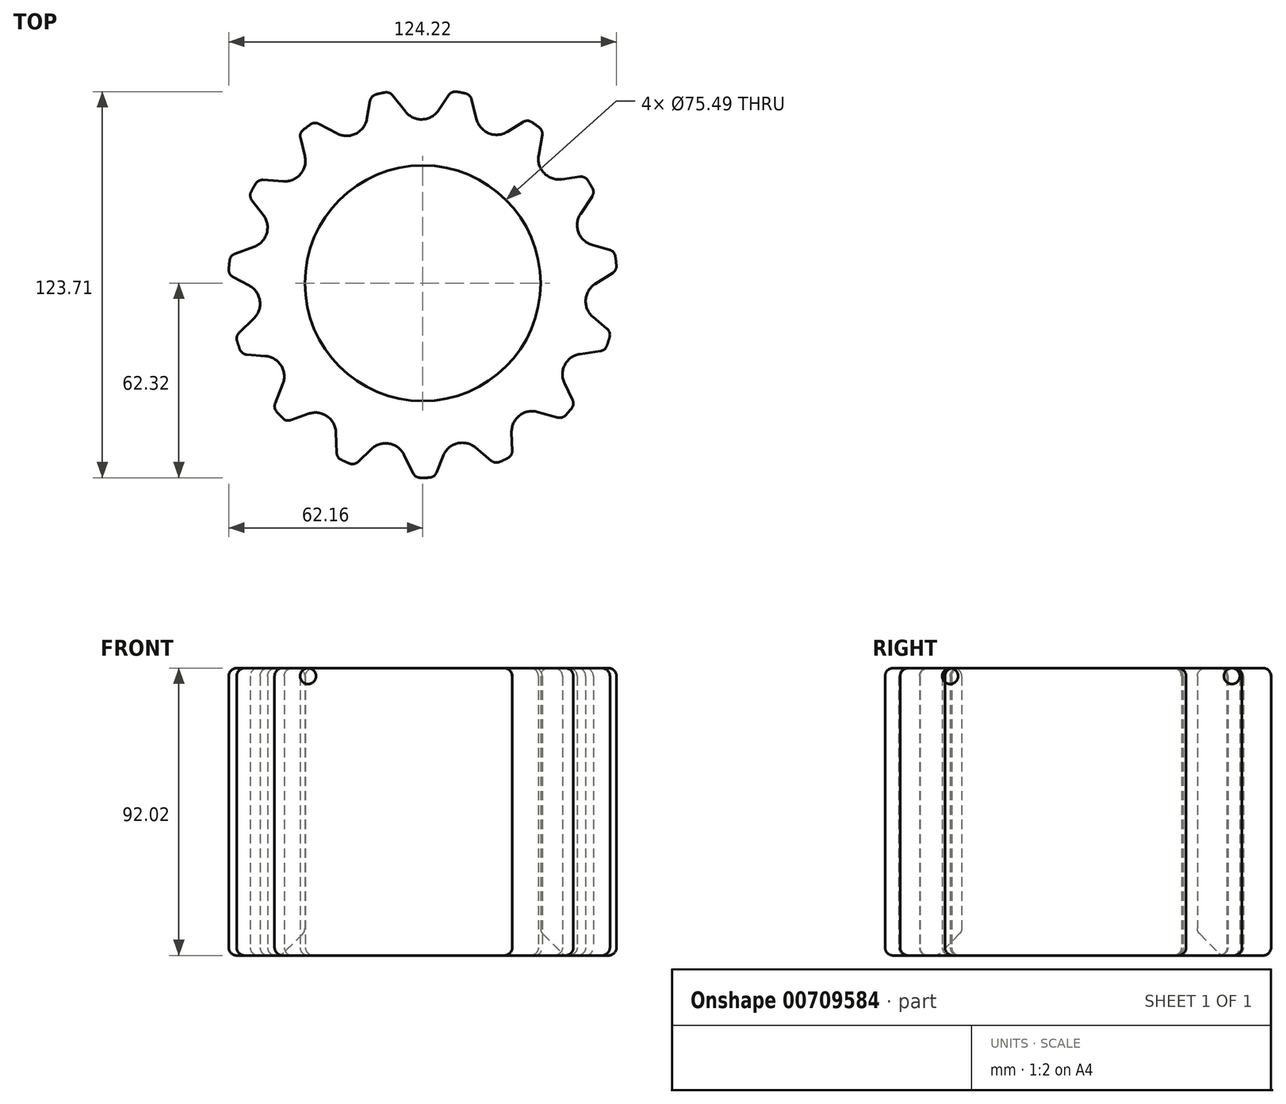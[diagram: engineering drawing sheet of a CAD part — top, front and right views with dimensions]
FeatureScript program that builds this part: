
annotation { "Feature Type Name" : "Feature", "Feature Type Description" : "" }
export const myFeature = defineFeature(function(context is Context, id is Id, definition is map)
    precondition{}
    {
        {
            var Q0;
            Q0=qCreatedBy(makeId("Top.planeOp"),FACE);
            var sketch = newSketch(context, id + "F0", { "sketchPlane" : qUnion([Q0])});
            skCircle(sketch, "E0", {"center": v(0, 0) * mm, "radius": 62.32 * mm});
            skLineSegment(sketch, "E1", {"start": v(-10.63, 61.4) * mm, "end": v(-5.56, 54.98) * mm});
            skLineSegment(sketch, "E2", {"start": v(5.04, 55.37) * mm, "end": v(9.28, 61.62) * mm});
            skLineSegment(sketch, "E3", {"start": v(9.28, 61.62) * mm, "end": v(9.28, 61.62) * mm});
            skPoint(sketch, "E4.visualSharp", {"position": v(0, 47.95) * mm});
            skArc(sketch, "E4.filletArc", {"start": v(-5.56, 54.98) * mm, "mid": v(-0.16, 52.5) * mm, "end": v(5.04, 55.37) * mm});
            skLineSegment(sketch, "E5", {"start": v(0, 113.38) * mm, "end": v(0, -82.74) * mm});
            skLineSegment(sketch, "E6", {"start": v(93.43, 0) * mm, "end": v(-91.25, 0) * mm});
            skLineSegment(sketch, "E7.anchor1", {"start": v(0, 0) * mm, "end": v(-5.56, 54.98) * mm, "construction": true});
            skLineSegment(sketch, "E7.anchor2", {"start": v(0, 0) * mm, "end": v(-5.56, 54.98) * mm, "construction": true});
            skArc(sketch, "E8.1.0", {"start": v(17.29, 52.5) * mm, "mid": v(21.2, 48.02) * mm, "end": v(27.12, 48.53) * mm});
            skLineSegment(sketch, "E8.1.1", {"start": v(27.12, 48.53) * mm, "end": v(33.54, 52.52) * mm});
            skLineSegment(sketch, "E8.1.2", {"start": v(15.26, 60.42) * mm, "end": v(17.29, 52.5) * mm});
            skArc(sketch, "E8.2.0", {"start": v(37.14, 40.92) * mm, "mid": v(38.9, 35.25) * mm, "end": v(44.52, 33.3) * mm});
            skLineSegment(sketch, "E8.2.1", {"start": v(44.52, 33.3) * mm, "end": v(52, 34.33) * mm});
            skLineSegment(sketch, "E8.2.2", {"start": v(38.52, 48.99) * mm, "end": v(37.14, 40.92) * mm});
            skArc(sketch, "E8.3.0", {"start": v(50.58, 22.28) * mm, "mid": v(49.87, 16.38) * mm, "end": v(54.21, 12.32) * mm});
            skLineSegment(sketch, "E8.3.1", {"start": v(54.21, 12.32) * mm, "end": v(61.47, 10.21) * mm});
            skLineSegment(sketch, "E8.3.2", {"start": v(55.11, 29.08) * mm, "end": v(50.58, 22.28) * mm});
            skArc(sketch, "E8.4.0", {"start": v(55.26, -0.22) * mm, "mid": v(52.22, -5.32) * mm, "end": v(54.54, -10.8) * mm});
            skLineSegment(sketch, "E8.4.1", {"start": v(54.54, -10.8) * mm, "end": v(60.31, -15.67) * mm});
            skLineSegment(sketch, "E8.4.2", {"start": v(62.18, 4.15) * mm, "end": v(55.26, -0.22) * mm});
            skArc(sketch, "E8.5.0", {"start": v(50.4, -22.68) * mm, "mid": v(45.54, -26.1) * mm, "end": v(45.43, -32.04) * mm});
            skLineSegment(sketch, "E8.5.1", {"start": v(45.43, -32.04) * mm, "end": v(48.72, -38.85) * mm});
            skLineSegment(sketch, "E8.5.2", {"start": v(58.5, -21.5) * mm, "end": v(50.4, -22.68) * mm});
            skArc(sketch, "E8.6.0", {"start": v(36.82, -41.22) * mm, "mid": v(30.99, -42.37) * mm, "end": v(28.47, -47.75) * mm});
            skLineSegment(sketch, "E8.6.1", {"start": v(28.47, -47.75) * mm, "end": v(28.71, -55.3) * mm});
            skLineSegment(sketch, "E8.6.2", {"start": v(44.7, -43.43) * mm, "end": v(36.82, -41.22) * mm});
            skArc(sketch, "E8.7.0", {"start": v(16.87, -52.63) * mm, "mid": v(11.07, -51.31) * mm, "end": v(6.59, -55.2) * mm});
            skLineSegment(sketch, "E8.7.1", {"start": v(6.59, -55.2) * mm, "end": v(3.73, -62.2) * mm});
            skLineSegment(sketch, "E8.7.2", {"start": v(23.16, -57.85) * mm, "end": v(16.87, -52.63) * mm});
            skArc(sketch, "E8.8.0", {"start": v(-6, -54.94) * mm, "mid": v(-10.75, -51.38) * mm, "end": v(-16.44, -53.11) * mm});
            skLineSegment(sketch, "E8.8.1", {"start": v(-16.44, -53.11) * mm, "end": v(-21.9, -58.34) * mm});
            skLineSegment(sketch, "E8.8.2", {"start": v(-2.37, -62.27) * mm, "end": v(-6, -54.94) * mm});
            skArc(sketch, "E8.9.0", {"start": v(-27.82, -47.75) * mm, "mid": v(-30.72, -42.56) * mm, "end": v(-36.62, -41.83) * mm});
            skLineSegment(sketch, "E8.9.1", {"start": v(-36.62, -41.83) * mm, "end": v(-43.73, -44.4) * mm});
            skLineSegment(sketch, "E8.9.2", {"start": v(-27.5, -55.92) * mm, "end": v(-27.82, -47.75) * mm});
            skArc(sketch, "E8.10.0", {"start": v(-44.84, -32.3) * mm, "mid": v(-45.38, -26.39) * mm, "end": v(-50.47, -23.32) * mm});
            skLineSegment(sketch, "E8.10.1", {"start": v(-50.47, -23.32) * mm, "end": v(-58, -22.77) * mm});
            skLineSegment(sketch, "E8.10.2", {"start": v(-47.86, -39.9) * mm, "end": v(-44.84, -32.3) * mm});
            skArc(sketch, "E8.11.0", {"start": v(-54.1, -11.27) * mm, "mid": v(-52.19, -5.65) * mm, "end": v(-55.6, -0.78) * mm});
            skLineSegment(sketch, "E8.11.1", {"start": v(-55.6, -0.78) * mm, "end": v(-62.25, 2.79) * mm});
            skLineSegment(sketch, "E8.11.2", {"start": v(-59.96, -16.99) * mm, "end": v(-54.1, -11.27) * mm});
            skArc(sketch, "E8.12.0", {"start": v(-54.01, 11.7) * mm, "mid": v(-49.97, 16.06) * mm, "end": v(-51.1, 21.9) * mm});
            skLineSegment(sketch, "E8.12.1", {"start": v(-51.1, 21.9) * mm, "end": v(-55.74, 27.87) * mm});
            skLineSegment(sketch, "E8.12.2", {"start": v(-61.68, 8.87) * mm, "end": v(-54.01, 11.7) * mm});
            skArc(sketch, "E8.13.0", {"start": v(-44.58, 32.66) * mm, "mid": v(-39.12, 35) * mm, "end": v(-37.78, 40.8) * mm});
            skLineSegment(sketch, "E8.13.1", {"start": v(-37.78, 40.8) * mm, "end": v(-39.58, 48.13) * mm});
            skLineSegment(sketch, "E8.13.2", {"start": v(-52.74, 33.19) * mm, "end": v(-44.58, 32.66) * mm});
            skArc(sketch, "E8.14.0", {"start": v(-27.44, 47.97) * mm, "mid": v(-21.5, 47.89) * mm, "end": v(-17.92, 52.63) * mm});
            skLineSegment(sketch, "E8.14.1", {"start": v(-17.92, 52.63) * mm, "end": v(-16.58, 60.07) * mm});
            skLineSegment(sketch, "E8.14.2", {"start": v(-34.69, 51.77) * mm, "end": v(-27.44, 47.97) * mm});
            skCircle(sketch, "E9", {"center": v(0, 0) * mm, "radius": 37.75 * mm});
            skSolve(sketch);
        }
        {
            var Q0;
            {var subQ1=sQuery(id+"F0.wireOp",EDGE,"E8.4.0");Q0=makeQuery(id+"F0.imprint","IMPRINT",FACE,{"disambiguationData":[TD([[makeQuery(id+"F0.imprint","IMPRINT",EDGE,{"derivedFrom":subQ1}),-1.0]])]});}
            var Q1;
            Q1=makeQuery(id+"F0.imprint","IMPRINT",FACE,{"disambiguationData":[TD([[makeQuery(id+"F0.imprint","IMPRINT",EDGE,{"derivedFrom":sQuery(id+"F0.wireOp",EDGE,"E8.8.0")}),-1.0]])]});
            var Q2;
            Q2=makeQuery(id+"F0.imprint","IMPRINT",FACE,{"disambiguationData":[TD([[makeQuery(id+"F0.imprint","IMPRINT",EDGE,{"derivedFrom":sQuery(id+"F0.wireOp",EDGE,"E8.1.0")}),-1.0]])]});
            var Q3;
            Q3=makeQuery(id+"F0.imprint","IMPRINT",FACE,{"disambiguationData":[TD([[makeQuery(id+"F0.imprint","IMPRINT",EDGE,{"derivedFrom":sQuery(id+"F0.wireOp",EDGE,"E8.12.0")}),-1.0]])]});
            extrude(context, id + "F1", {"entities" : qUnion([Q0, Q1, Q2, Q3]), "depth" : 92.02 * mm, "offsetDistance" : 25.4 * mm});
        }
        {
            var Q0;
            Q0=makeQuery(id+"F1.opExtrude","CAP_EDGE",EDGE,{"disambiguationData":[OSD([sQuery(id+"F0.wireOp",EDGE,"E9")])],"isStart":true});
            chamfer(context, id + "F2", {"entities" : qUnion([Q0]), "width" : 7.62 * mm, "tangentPropagation" : true});
        }
        {
            var Q0;
            Q0=makeQuery(id+"F1.opExtrude","SWEPT_EDGE",EDGE,{"disambiguationData":[OSD([sQuery(id+"F0.wireOp",EDGE,"E0"),sQuery(id+"F0.wireOp",EDGE,"E8.12.2")])]});
            var Q1;
            Q1=makeQuery(id+"F1.opExtrude","SWEPT_EDGE",EDGE,{"disambiguationData":[OSD([sQuery(id+"F0.wireOp",EDGE,"E0"),sQuery(id+"F0.wireOp",EDGE,"E8.11.1")])]});
            var Q2;
            Q2=makeQuery(id+"F1.opExtrude","SWEPT_EDGE",EDGE,{"disambiguationData":[OSD([sQuery(id+"F0.wireOp",EDGE,"E0"),sQuery(id+"F0.wireOp",EDGE,"E8.12.1")])]});
            var Q3;
            Q3=makeQuery(id+"F1.opExtrude","SWEPT_EDGE",EDGE,{"disambiguationData":[OSD([sQuery(id+"F0.wireOp",EDGE,"E0"),sQuery(id+"F0.wireOp",EDGE,"E8.13.2")])]});
            var Q4;
            Q4=makeQuery(id+"F1.opExtrude","SWEPT_EDGE",EDGE,{"disambiguationData":[OSD([sQuery(id+"F0.wireOp",EDGE,"E0"),sQuery(id+"F0.wireOp",EDGE,"E8.13.1")])]});
            var Q5;
            Q5=makeQuery(id+"F1.opExtrude","SWEPT_EDGE",EDGE,{"disambiguationData":[OSD([sQuery(id+"F0.wireOp",EDGE,"E0"),sQuery(id+"F0.wireOp",EDGE,"E8.14.2")])]});
            var Q6;
            Q6=makeQuery(id+"F1.opExtrude","SWEPT_EDGE",EDGE,{"disambiguationData":[OSD([sQuery(id+"F0.wireOp",EDGE,"E0"),sQuery(id+"F0.wireOp",EDGE,"E8.14.1")])]});
            var Q7;
            Q7=makeQuery(id+"F1.opExtrude","SWEPT_EDGE",EDGE,{"disambiguationData":[OSD([sQuery(id+"F0.wireOp",EDGE,"E0"),sQuery(id+"F0.wireOp",EDGE,"E1")])]});
            var Q8;
            Q8=makeQuery(id+"F1.opExtrude","SWEPT_EDGE",EDGE,{"disambiguationData":[OSD([sQuery(id+"F0.wireOp",EDGE,"E0"),sQuery(id+"F0.wireOp",EDGE,"E2")])]});
            var Q9;
            Q9=makeQuery(id+"F1.opExtrude","SWEPT_EDGE",EDGE,{"disambiguationData":[OSD([sQuery(id+"F0.wireOp",EDGE,"E0"),sQuery(id+"F0.wireOp",EDGE,"E8.1.2")])]});
            var Q10;
            Q10=makeQuery(id+"F1.opExtrude","SWEPT_EDGE",EDGE,{"disambiguationData":[OSD([sQuery(id+"F0.wireOp",EDGE,"E0"),sQuery(id+"F0.wireOp",EDGE,"E8.1.1")])]});
            var Q11;
            Q11=makeQuery(id+"F1.opExtrude","SWEPT_EDGE",EDGE,{"disambiguationData":[OSD([sQuery(id+"F0.wireOp",EDGE,"E0"),sQuery(id+"F0.wireOp",EDGE,"E8.2.2")])]});
            var Q12;
            Q12=makeQuery(id+"F1.opExtrude","SWEPT_EDGE",EDGE,{"disambiguationData":[OSD([sQuery(id+"F0.wireOp",EDGE,"E0"),sQuery(id+"F0.wireOp",EDGE,"E8.3.2")])]});
            var Q13;
            Q13=makeQuery(id+"F1.opExtrude","SWEPT_EDGE",EDGE,{"disambiguationData":[OSD([sQuery(id+"F0.wireOp",EDGE,"E0"),sQuery(id+"F0.wireOp",EDGE,"E8.2.1")])]});
            var Q14;
            Q14=makeQuery(id+"F1.opExtrude","SWEPT_EDGE",EDGE,{"disambiguationData":[OSD([sQuery(id+"F0.wireOp",EDGE,"E0"),sQuery(id+"F0.wireOp",EDGE,"E8.3.1")])]});
            var Q15;
            Q15=makeQuery(id+"F1.opExtrude","SWEPT_EDGE",EDGE,{"disambiguationData":[OSD([sQuery(id+"F0.wireOp",EDGE,"E0"),sQuery(id+"F0.wireOp",EDGE,"E8.4.2")])]});
            var Q16;
            Q16=makeQuery(id+"F1.opExtrude","SWEPT_EDGE",EDGE,{"disambiguationData":[OSD([sQuery(id+"F0.wireOp",EDGE,"E0"),sQuery(id+"F0.wireOp",EDGE,"E8.4.1")])]});
            var Q17;
            Q17=makeQuery(id+"F1.opExtrude","SWEPT_EDGE",EDGE,{"disambiguationData":[OSD([sQuery(id+"F0.wireOp",EDGE,"E0"),sQuery(id+"F0.wireOp",EDGE,"E8.5.2")])]});
            var Q18;
            Q18=makeQuery(id+"F1.opExtrude","SWEPT_EDGE",EDGE,{"disambiguationData":[OSD([sQuery(id+"F0.wireOp",EDGE,"E0"),sQuery(id+"F0.wireOp",EDGE,"E8.6.2")])]});
            var Q19;
            Q19=makeQuery(id+"F1.opExtrude","SWEPT_EDGE",EDGE,{"disambiguationData":[OSD([sQuery(id+"F0.wireOp",EDGE,"E0"),sQuery(id+"F0.wireOp",EDGE,"E8.5.1")])]});
            var Q20;
            Q20=makeQuery(id+"F1.opExtrude","SWEPT_EDGE",EDGE,{"disambiguationData":[OSD([sQuery(id+"F0.wireOp",EDGE,"E0"),sQuery(id+"F0.wireOp",EDGE,"E8.6.1")])]});
            var Q21;
            Q21=makeQuery(id+"F1.opExtrude","SWEPT_EDGE",EDGE,{"disambiguationData":[OSD([sQuery(id+"F0.wireOp",EDGE,"E0"),sQuery(id+"F0.wireOp",EDGE,"E8.7.2")])]});
            var Q22;
            Q22=makeQuery(id+"F1.opExtrude","SWEPT_EDGE",EDGE,{"disambiguationData":[OSD([sQuery(id+"F0.wireOp",EDGE,"E0"),sQuery(id+"F0.wireOp",EDGE,"E8.7.1")])]});
            var Q23;
            Q23=makeQuery(id+"F1.opExtrude","SWEPT_EDGE",EDGE,{"disambiguationData":[OSD([sQuery(id+"F0.wireOp",EDGE,"E0"),sQuery(id+"F0.wireOp",EDGE,"E8.8.2")])]});
            var Q24;
            Q24=makeQuery(id+"F1.opExtrude","SWEPT_EDGE",EDGE,{"disambiguationData":[OSD([sQuery(id+"F0.wireOp",EDGE,"E0"),sQuery(id+"F0.wireOp",EDGE,"E8.9.2")])]});
            var Q25;
            Q25=makeQuery(id+"F1.opExtrude","SWEPT_EDGE",EDGE,{"disambiguationData":[OSD([sQuery(id+"F0.wireOp",EDGE,"E0"),sQuery(id+"F0.wireOp",EDGE,"E8.8.1")])]});
            var Q26;
            Q26=makeQuery(id+"F1.opExtrude","SWEPT_EDGE",EDGE,{"disambiguationData":[OSD([sQuery(id+"F0.wireOp",EDGE,"E0"),sQuery(id+"F0.wireOp",EDGE,"E8.9.1")])]});
            var Q27;
            Q27=makeQuery(id+"F1.opExtrude","SWEPT_EDGE",EDGE,{"disambiguationData":[OSD([sQuery(id+"F0.wireOp",EDGE,"E0"),sQuery(id+"F0.wireOp",EDGE,"E8.10.2")])]});
            var Q28;
            Q28=makeQuery(id+"F1.opExtrude","SWEPT_EDGE",EDGE,{"disambiguationData":[OSD([sQuery(id+"F0.wireOp",EDGE,"E0"),sQuery(id+"F0.wireOp",EDGE,"E8.10.1")])]});
            var Q29;
            Q29=makeQuery(id+"F1.opExtrude","SWEPT_EDGE",EDGE,{"disambiguationData":[OSD([sQuery(id+"F0.wireOp",EDGE,"E0"),sQuery(id+"F0.wireOp",EDGE,"E8.11.2")])]});
            fillet(context, id + "F3", {"entities" : qUnion([Q0, Q1, Q2, Q3, Q4, Q5, Q6, Q7, Q8, Q9, Q10, Q11, Q12, Q13, Q14, Q15, Q16, Q17, Q18, Q19, Q20, Q21, Q22, Q23, Q24, Q25, Q26, Q27, Q28, Q29]), "radius" : 2.54 * mm, "tangentPropagation" : true, "allowEdgeOverflow" : false});
        }
        {
            var Q0;
            Q0=makeQuery(id+"F1.opExtrude","CAP_FACE",FACE,{"disambiguationData":[OSD([sQuery(id+"F0.wireOp",EDGE,"E0"),sQuery(id+"F0.wireOp",EDGE,"E8.1.0"),sQuery(id+"F0.wireOp",EDGE,"E8.1.1"),sQuery(id+"F0.wireOp",EDGE,"E8.1.2"),sQuery(id+"F0.wireOp",EDGE,"E8.2.0"),sQuery(id+"F0.wireOp",EDGE,"E8.2.1"),sQuery(id+"F0.wireOp",EDGE,"E8.2.2"),sQuery(id+"F0.wireOp",EDGE,"E8.3.0"),sQuery(id+"F0.wireOp",EDGE,"E8.3.1"),sQuery(id+"F0.wireOp",EDGE,"E8.3.2"),sQuery(id+"F0.wireOp",EDGE,"E8.4.0"),sQuery(id+"F0.wireOp",EDGE,"E8.4.1"),sQuery(id+"F0.wireOp",EDGE,"E8.4.2"),sQuery(id+"F0.wireOp",EDGE,"E8.5.0"),sQuery(id+"F0.wireOp",EDGE,"E8.5.1"),sQuery(id+"F0.wireOp",EDGE,"E8.5.2"),sQuery(id+"F0.wireOp",EDGE,"E8.6.0"),sQuery(id+"F0.wireOp",EDGE,"E8.6.1"),sQuery(id+"F0.wireOp",EDGE,"E8.6.2"),sQuery(id+"F0.wireOp",EDGE,"E8.7.0"),sQuery(id+"F0.wireOp",EDGE,"E8.7.1"),sQuery(id+"F0.wireOp",EDGE,"E8.7.2"),sQuery(id+"F0.wireOp",EDGE,"E8.8.0"),sQuery(id+"F0.wireOp",EDGE,"E8.8.1"),sQuery(id+"F0.wireOp",EDGE,"E8.8.2"),sQuery(id+"F0.wireOp",EDGE,"E8.9.0"),sQuery(id+"F0.wireOp",EDGE,"E8.9.1"),sQuery(id+"F0.wireOp",EDGE,"E8.9.2"),sQuery(id+"F0.wireOp",EDGE,"E8.10.0"),sQuery(id+"F0.wireOp",EDGE,"E8.10.1"),sQuery(id+"F0.wireOp",EDGE,"E8.10.2"),sQuery(id+"F0.wireOp",EDGE,"E8.11.0"),sQuery(id+"F0.wireOp",EDGE,"E8.11.1"),sQuery(id+"F0.wireOp",EDGE,"E8.11.2"),sQuery(id+"F0.wireOp",EDGE,"E8.12.0"),sQuery(id+"F0.wireOp",EDGE,"E8.12.1"),sQuery(id+"F0.wireOp",EDGE,"E8.12.2"),sQuery(id+"F0.wireOp",EDGE,"E8.13.0"),sQuery(id+"F0.wireOp",EDGE,"E8.13.1"),sQuery(id+"F0.wireOp",EDGE,"E8.13.2"),sQuery(id+"F0.wireOp",EDGE,"E8.14.0"),sQuery(id+"F0.wireOp",EDGE,"E8.14.1"),sQuery(id+"F0.wireOp",EDGE,"E8.14.2"),sQuery(id+"F0.wireOp",EDGE,"E4.filletArc"),sQuery(id+"F0.wireOp",EDGE,"E2"),sQuery(id+"F0.wireOp",EDGE,"E1"),sQuery(id+"F0.wireOp",EDGE,"E9")])],"isStart":false});
            fillet(context, id + "F4", {"entities" : qUnion([Q0]), "radius" : 2.54 * mm, "tangentPropagation" : true, "allowEdgeOverflow" : false});
        }
        {
            var Q0;
            Q0=makeQuery(id+"F1.opExtrude","CAP_FACE",FACE,{"disambiguationData":[OSD([sQuery(id+"F0.wireOp",EDGE,"E0"),sQuery(id+"F0.wireOp",EDGE,"E8.1.0"),sQuery(id+"F0.wireOp",EDGE,"E8.1.1"),sQuery(id+"F0.wireOp",EDGE,"E8.1.2"),sQuery(id+"F0.wireOp",EDGE,"E8.2.0"),sQuery(id+"F0.wireOp",EDGE,"E8.2.1"),sQuery(id+"F0.wireOp",EDGE,"E8.2.2"),sQuery(id+"F0.wireOp",EDGE,"E8.3.0"),sQuery(id+"F0.wireOp",EDGE,"E8.3.1"),sQuery(id+"F0.wireOp",EDGE,"E8.3.2"),sQuery(id+"F0.wireOp",EDGE,"E8.4.0"),sQuery(id+"F0.wireOp",EDGE,"E8.4.1"),sQuery(id+"F0.wireOp",EDGE,"E8.4.2"),sQuery(id+"F0.wireOp",EDGE,"E8.5.0"),sQuery(id+"F0.wireOp",EDGE,"E8.5.1"),sQuery(id+"F0.wireOp",EDGE,"E8.5.2"),sQuery(id+"F0.wireOp",EDGE,"E8.6.0"),sQuery(id+"F0.wireOp",EDGE,"E8.6.1"),sQuery(id+"F0.wireOp",EDGE,"E8.6.2"),sQuery(id+"F0.wireOp",EDGE,"E8.7.0"),sQuery(id+"F0.wireOp",EDGE,"E8.7.1"),sQuery(id+"F0.wireOp",EDGE,"E8.7.2"),sQuery(id+"F0.wireOp",EDGE,"E8.8.0"),sQuery(id+"F0.wireOp",EDGE,"E8.8.1"),sQuery(id+"F0.wireOp",EDGE,"E8.8.2"),sQuery(id+"F0.wireOp",EDGE,"E8.9.0"),sQuery(id+"F0.wireOp",EDGE,"E8.9.1"),sQuery(id+"F0.wireOp",EDGE,"E8.9.2"),sQuery(id+"F0.wireOp",EDGE,"E8.10.0"),sQuery(id+"F0.wireOp",EDGE,"E8.10.1"),sQuery(id+"F0.wireOp",EDGE,"E8.10.2"),sQuery(id+"F0.wireOp",EDGE,"E8.11.0"),sQuery(id+"F0.wireOp",EDGE,"E8.11.1"),sQuery(id+"F0.wireOp",EDGE,"E8.11.2"),sQuery(id+"F0.wireOp",EDGE,"E8.12.0"),sQuery(id+"F0.wireOp",EDGE,"E8.12.1"),sQuery(id+"F0.wireOp",EDGE,"E8.12.2"),sQuery(id+"F0.wireOp",EDGE,"E8.13.0"),sQuery(id+"F0.wireOp",EDGE,"E8.13.1"),sQuery(id+"F0.wireOp",EDGE,"E8.13.2"),sQuery(id+"F0.wireOp",EDGE,"E8.14.0"),sQuery(id+"F0.wireOp",EDGE,"E8.14.1"),sQuery(id+"F0.wireOp",EDGE,"E8.14.2"),sQuery(id+"F0.wireOp",EDGE,"E4.filletArc"),sQuery(id+"F0.wireOp",EDGE,"E2"),sQuery(id+"F0.wireOp",EDGE,"E1"),sQuery(id+"F0.wireOp",EDGE,"E9")])],"isStart":true});
            var Q1;
            {var subQ0=sQuery(id+"F0.wireOp",EDGE,"E9");Q1=makeQuery(id+"F2.opChamfer","BLEND_EDGE",EDGE,{"blendedFrom":[makeQuery(id+"F1.opExtrude","CAP_EDGE",EDGE,{"disambiguationData":[OSD([subQ0])],"isStart":true}),makeQuery(id+"F1.opExtrude","SWEPT_FACE",FACE,{"disambiguationData":[OSD([subQ0])]})],"blendedInto":[makeQuery(id+"F1.opExtrude","SWEPT_FACE",FACE,{"disambiguationData":[OSD([subQ0])]})]});}
            fillet(context, id + "F5", {"entities" : qUnion([Q0, Q1]), "radius" : 2.54 * mm, "tangentPropagation" : true, "allowEdgeOverflow" : false});
        }
    });
